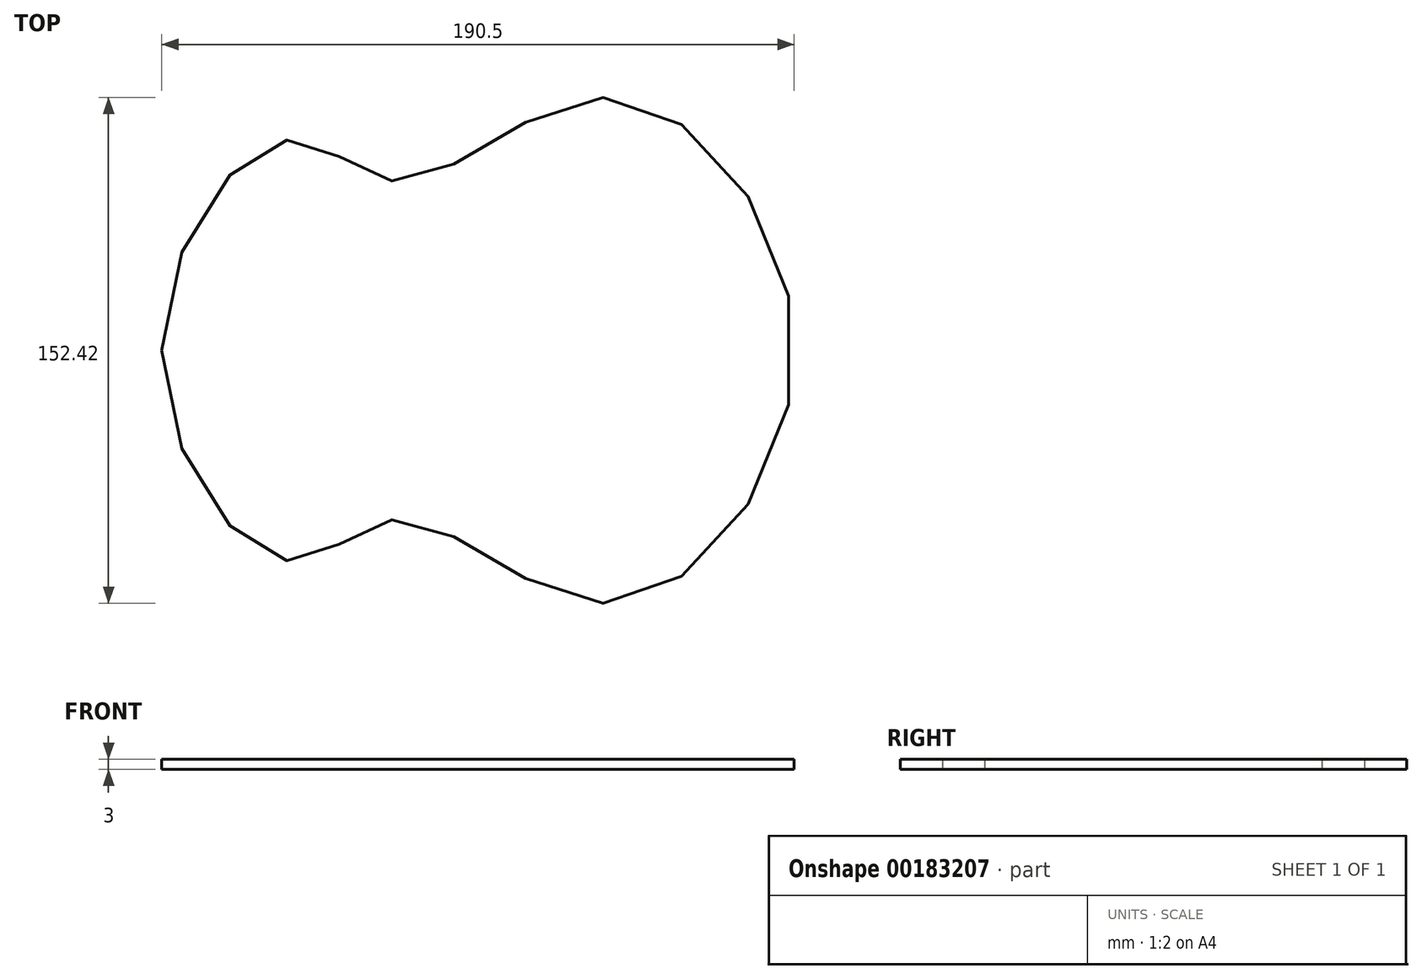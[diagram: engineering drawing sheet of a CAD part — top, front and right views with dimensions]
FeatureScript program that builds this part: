
annotation { "Feature Type Name" : "Feature", "Feature Type Description" : "" }
export const myFeature = defineFeature(function(context is Context, id is Id, definition is map)
    precondition{}
    {
        {
            var Q0;
            Q0=qCreatedBy(makeId("Top.planeOp"),FACE);
            var sketch = newSketch(context, id + "F0", { "sketchPlane" : qUnion([Q0])});
            skLineSegment(sketch, "E0", {"start": v(-85.18, 0) * mm, "end": v(105.32, 0) * mm, "construction": true});
            skLineSegment(sketch, "E1", {"start": v(49.21, 0) * mm, "end": v(49.21, 76.2) * mm, "construction": true});
            skLineSegment(sketch, "E2", {"start": v(49.21, 0) * mm, "end": v(49.21, -76.2) * mm, "construction": true});
            skLineSegment(sketch, "E3", {"start": v(-13.14, 0) * mm, "end": v(-13.14, 50.8) * mm, "construction": true});
            skLineSegment(sketch, "E4", {"start": v(-13.14, 0) * mm, "end": v(-13.14, -50.8) * mm, "construction": true});
            skLineSegment(sketch, "E5", {"start": v(-46.72, 0) * mm, "end": v(-46.72, 63.5) * mm, "construction": true});
            skLineSegment(sketch, "E6", {"start": v(-46.72, 0) * mm, "end": v(-46.72, -63.5) * mm, "construction": true});
            skFitSpline(sketch, "E7", {"points": [v(-85.18, 0) * mm, v(-46.72, 63.5) * mm, v(-13.14, 50.8) * mm, v(49.21, 76.2) * mm, v(105.32, 0) * mm, v(49.21, -76.2) * mm, v(-13.14, -50.8) * mm, v(-46.72, -63.5) * mm, v(-85.18, 0) * mm]});
            skSolve(sketch);
        }
        {
            var Q0;
            Q0=makeQuery(id+"F0.imprint","IMPRINT",FACE,{"disambiguationData":[TD([[makeQuery(id+"F0.imprint","IMPRINT",EDGE,{"derivedFrom":sQuery(id+"F0.wireOp",EDGE,"E7")}),-1.0]])]});
            var Q1;
            Q1=sQuery(id+"F0.wireOp",EDGE,"E7");
            extrude(context, id + "F1", {"entities" : qUnion([Q0]), "surfaceEntities" : qUnion([Q1]), "depth" : 3 * mm});
        }
    });
